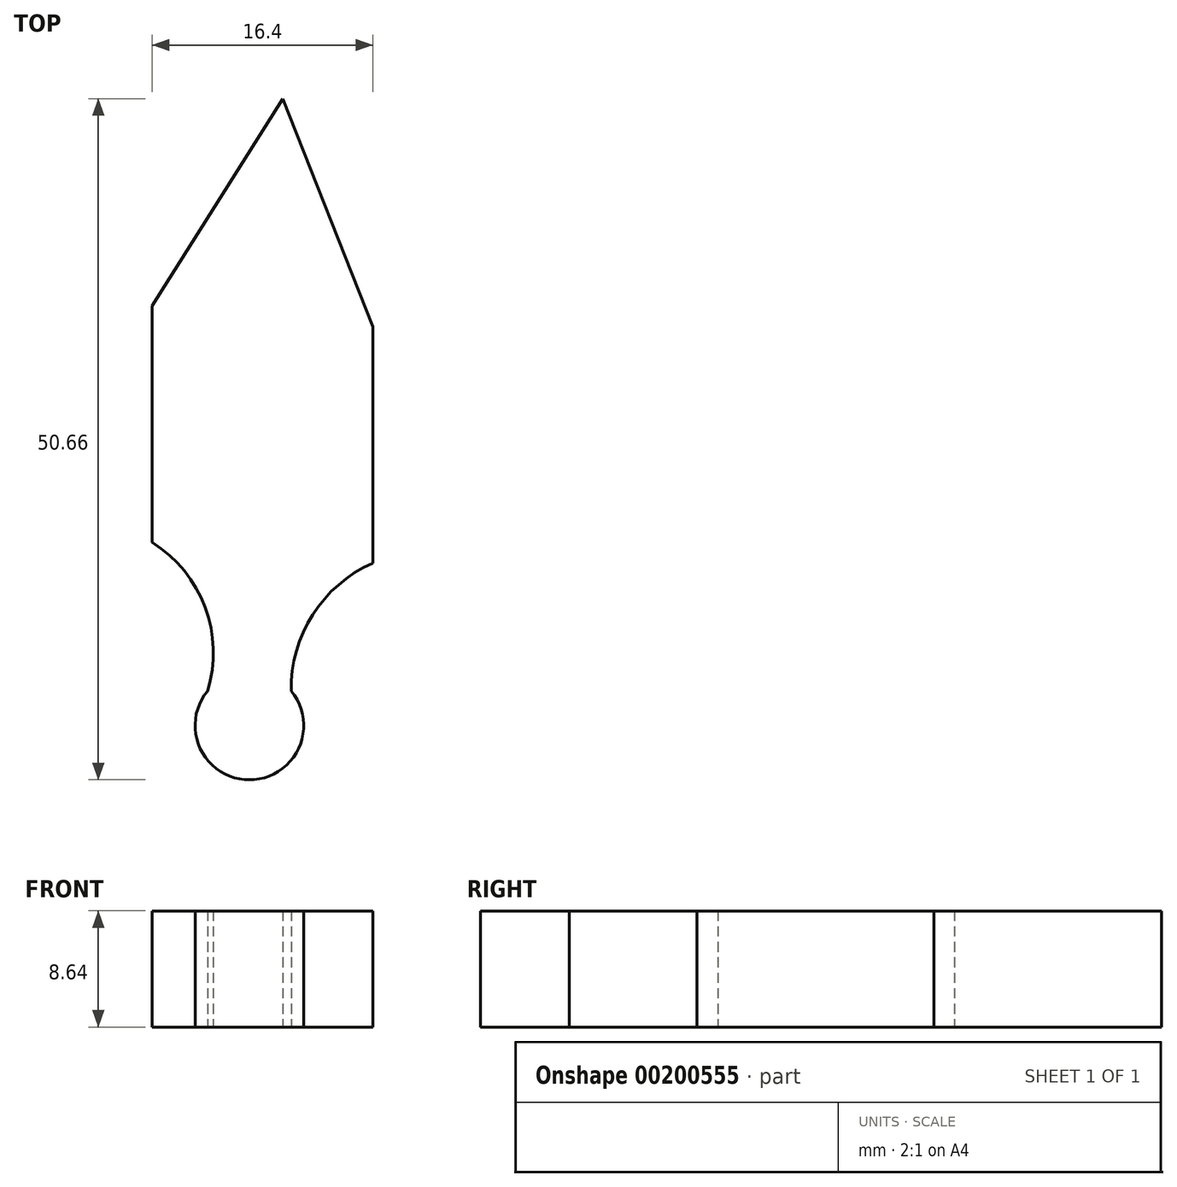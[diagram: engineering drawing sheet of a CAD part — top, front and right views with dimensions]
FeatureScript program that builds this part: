
annotation { "Feature Type Name" : "Feature", "Feature Type Description" : "" }
export const myFeature = defineFeature(function(context is Context, id is Id, definition is map)
    precondition{}
    {
        {
            var Q0;
            Q0=qCreatedBy(makeId("Top.planeOp"),FACE);
            var sketch = newSketch(context, id + "F0", { "sketchPlane" : qUnion([Q0])});
            skLineSegment(sketch, "E0", {"start": v(-51.4, 28.66) * mm, "end": v(-41.68, 44.06) * mm});
            skLineSegment(sketch, "E1", {"start": v(-41.68, 44.06) * mm, "end": v(-35, 27.11) * mm});
            skLineSegment(sketch, "E2", {"start": v(-51.4, 28.66) * mm, "end": v(-51.4, 11.06) * mm});
            skLineSegment(sketch, "E3", {"start": v(-35, 27.11) * mm, "end": v(-35, 9.51) * mm});
            skArc(sketch, "E4", {"start": v(-47.3, 0) * mm, "mid": v(-47.46, 6.23) * mm, "end": v(-51.4, 11.06) * mm});
            skArc(sketch, "E5", {"start": v(-35, 9.51) * mm, "mid": v(-39.47, 5.67) * mm, "end": v(-41.06, 0) * mm});
            skArc(sketch, "E6", {"start": v(-47.3, 0) * mm, "mid": v(-44.18, -6.6) * mm, "end": v(-41.06, 0) * mm});
            skSolve(sketch);
        }
        {
            var Q0;
            Q0 = qSketchRegion(id + "F0", true);
            extrude(context, id + "F1", {"entities" : qUnion([Q0]), "depth" : 8.64 * mm});
        }
    });
